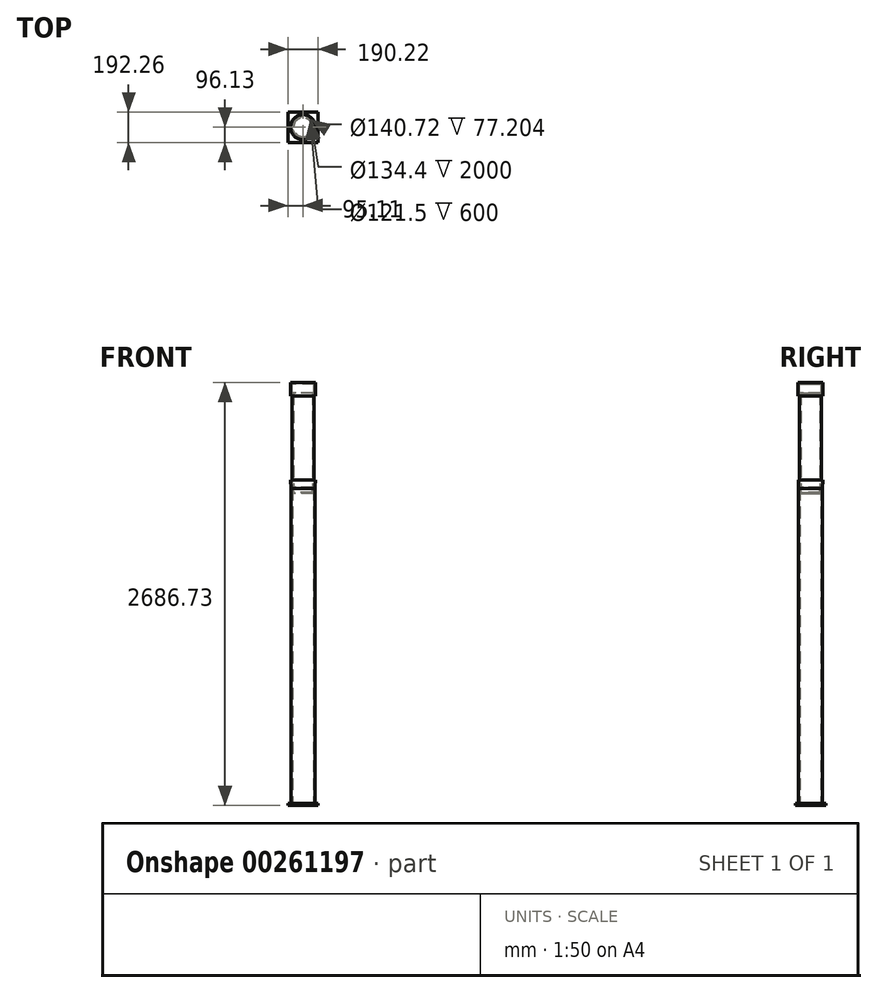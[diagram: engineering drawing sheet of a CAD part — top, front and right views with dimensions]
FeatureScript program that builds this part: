
annotation { "Feature Type Name" : "Feature", "Feature Type Description" : "" }
export const myFeature = defineFeature(function(context is Context, id is Id, definition is map)
    precondition{}
    {
        {
            var Q0;
            Q0=qCreatedBy(makeId("Top.planeOp"),FACE);
            var sketch = newSketch(context, id + "F0", { "sketchPlane" : qUnion([Q0])});
            skCircle(sketch, "E0", {"center": v(0, 0) * mm, "radius": 76.2 * mm});
            skCircle(sketch, "E1", {"center": v(0, 0) * mm, "radius": 67.2 * mm});
            skSolve(sketch);
        }
        {
            var Q0;
            Q0 = qSketchRegion(id + "F0", true);
            extrude(context, id + "F1", {"entities" : qUnion([Q0]), "depth" : 2000 * mm});
        }
        {
            var Q0;
            Q0=qCreatedBy(makeId("Top.planeOp"),FACE);
            var sketch = newSketch(context, id + "F2", { "sketchPlane" : qUnion([Q0])});
            skLineSegment(sketch, "E2.bottom", {"start": v(95.1, -96.13) * mm, "end": v(-95.1, -96.13) * mm});
            skLineSegment(sketch, "E2.top", {"start": v(95.1, 96.13) * mm, "end": v(-95.1, 96.13) * mm});
            skLineSegment(sketch, "E2.left", {"start": v(95.1, -96.13) * mm, "end": v(95.1, 96.13) * mm});
            skLineSegment(sketch, "E2.right", {"start": v(-95.1, -96.13) * mm, "end": v(-95.1, 96.13) * mm});
            skPoint(sketch, "E2.middle", {"position": v(0, 0) * mm});
            skSolve(sketch);
        }
        {
            var Q0;
            Q0 = qSketchRegion(id + "F2", true);
            extrude(context, id + "F3", {"entities" : qUnion([Q0]), "operationType" : NewBodyOperationType.ADD, "oppositeDirection" : true, "depth" : 12.7 * mm});
        }
        {
            var Q0;
            Q0=qCreatedBy(makeId("Right.planeOp"),FACE);
            var sketch = newSketch(context, id + "F4", { "sketchPlane" : qUnion([Q0])});
            skLineSegment(sketch, "E3", {"start": v(75.94, 2000.1) * mm, "end": v(66.94, 2000.1) * mm});
            skLineSegment(sketch, "E4", {"start": v(61.9, 1971.02) * mm, "end": v(61.43, 1971) * mm});
            skLineSegment(sketch, "E5.1", {"start": v(69.86, 2006.4) * mm, "end": v(60.75, 2006.4) * mm});
            skLineSegment(sketch, "E5.2", {"start": v(61.43, 1971.02) * mm, "end": v(61.43, 1971) * mm});
            skLineSegment(sketch, "E6", {"start": v(61.9, 1971.02) * mm, "end": v(61.43, 1971.02) * mm});
            skLineSegment(sketch, "E7", {"start": v(0, 2061.67) * mm, "end": v(0, 2005.03) * mm, "construction": true});
            skLineSegment(sketch, "E8", {"start": v(66.94, 2000.1) * mm, "end": v(66.14, 1969.8) * mm});
            skLineSegment(sketch, "E9.0", {"start": v(60.75, 2006.4) * mm, "end": v(59.96, 1976.15) * mm});
            skLineSegment(sketch, "E10", {"start": v(75.94, 2000.1) * mm, "end": v(78.32, 2054.29) * mm});
            skLineSegment(sketch, "E11", {"start": v(66.14, 1969.8) * mm, "end": v(0, 1969.8) * mm});
            skLineSegment(sketch, "E12.0", {"start": v(59.96, 1976.15) * mm, "end": v(0, 1976.15) * mm});
            skLineSegment(sketch, "E13.0", {"start": v(69.86, 2006.4) * mm, "end": v(71.96, 2054.29) * mm});
            skLineSegment(sketch, "E14", {"start": v(78.32, 2054.29) * mm, "end": v(71.96, 2054.29) * mm});
            skLineSegment(sketch, "E15", {"start": v(0, 1976.15) * mm, "end": v(0, 1969.8) * mm});
            skSolve(sketch);
        }
        {
            var Q0;
            Q0 = qSketchRegion(id + "F4", true);
            var Q1;
            Q1=sQuery(id+"F4.wireOp",EDGE,"E7");
            revolve(context, id + "F5", {"entities" : qUnion([Q0]), "axis" : qUnion([Q1]), "revolveType" : RevolveType.FULL});
        }
        {
            var Q0;
            Q0=makeQuery(id+"F5.opRevolve","SWEPT_FACE",FACE,{"disambiguationData":[OSD([sQuery(id+"F4.wireOp",EDGE,"E5.1")])]});
            extrude(context, id + "F6", {"entities" : qUnion([Q0]), "depth" : 600 * mm});
        }
        {
            var Q0;
            Q0=qCreatedBy(makeId("Right.planeOp"),FACE);
            var sketch = newSketch(context, id + "F7", { "sketchPlane" : qUnion([Q0])});
            skLineSegment(sketch, "E16", {"start": v(70.36, 2588.15) * mm, "end": v(79.34, 2588.15) * mm});
            skLineSegment(sketch, "E17", {"start": v(79.34, 2588.15) * mm, "end": v(79.34, 2674.03) * mm});
            skLineSegment(sketch, "E18", {"start": v(79.34, 2674.03) * mm, "end": v(0, 2674.03) * mm});
            skLineSegment(sketch, "E19", {"start": v(0, 2674.03) * mm, "end": v(0, 2665.35) * mm});
            skLineSegment(sketch, "E20", {"start": v(0, 2665.35) * mm, "end": v(70.36, 2665.35) * mm});
            skLineSegment(sketch, "E21", {"start": v(70.36, 2665.35) * mm, "end": v(70.36, 2588.15) * mm});
            skSolve(sketch);
        }
        {
            var Q0;
            Q0 = qSketchRegion(id + "F7", true);
            var Q1;
            Q1=sQuery(id+"F7.wireOp",EDGE,"E19");
            revolve(context, id + "F8", {"entities" : qUnion([Q0]), "axis" : qUnion([Q1]), "revolveType" : RevolveType.FULL});
        }
    });
